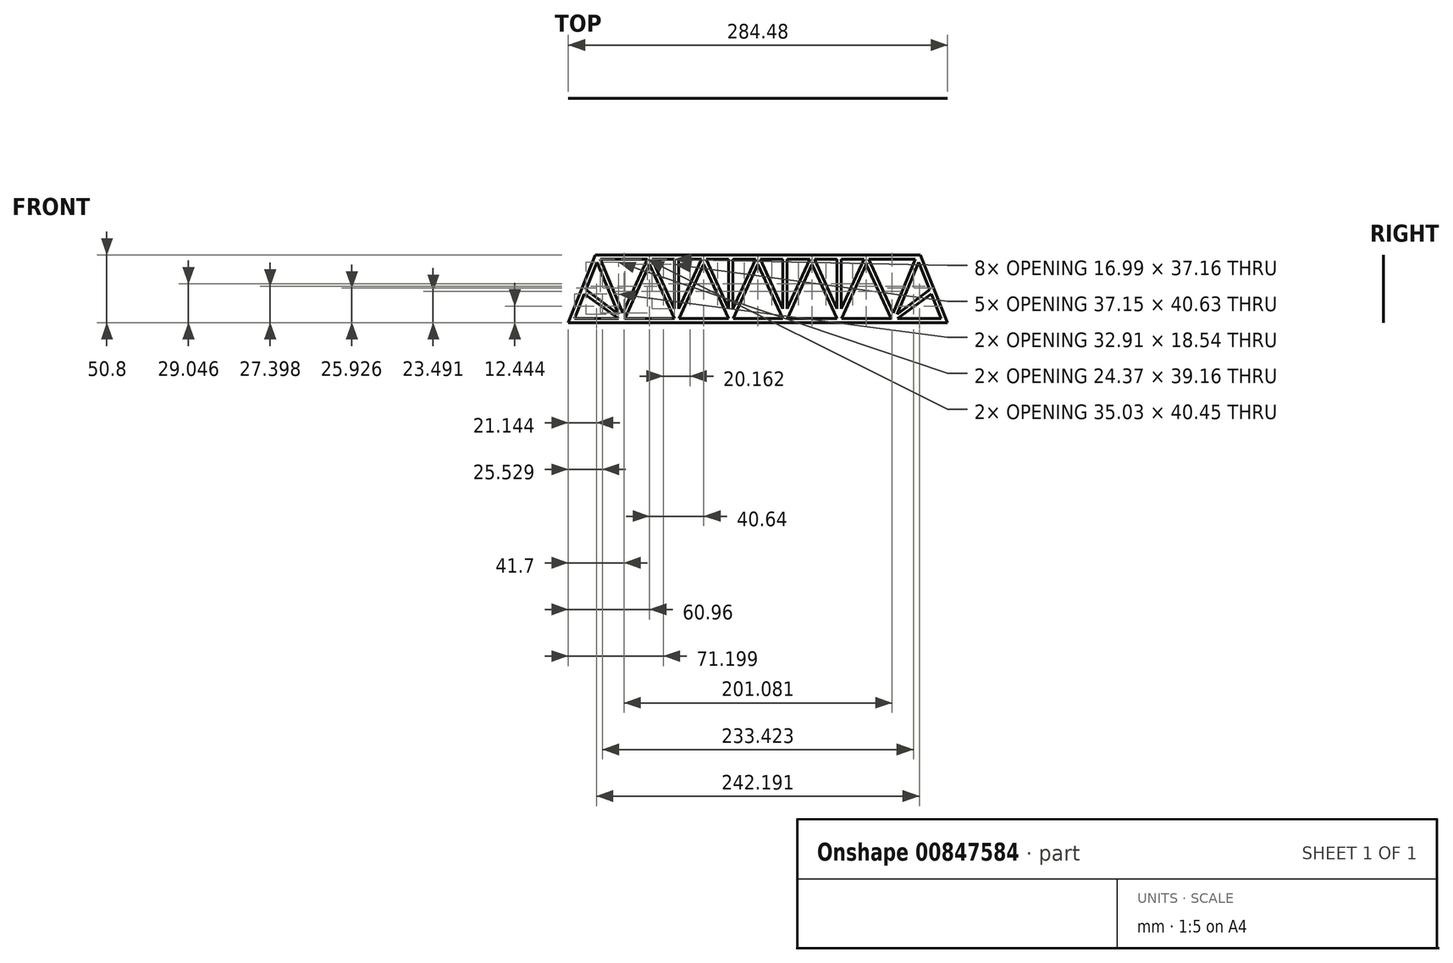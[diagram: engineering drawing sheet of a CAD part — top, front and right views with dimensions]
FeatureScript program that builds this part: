
annotation { "Feature Type Name" : "Feature", "Feature Type Description" : "" }
export const myFeature = defineFeature(function(context is Context, id is Id, definition is map)
    precondition{}
    {
        {
            var Q0;
            Q0=qCreatedBy(makeId("Front.planeOp"),FACE);
            var sketch = newSketch(context, id + "F0", { "sketchPlane" : qUnion([Q0])});
            skLineSegment(sketch, "E0.left", {"start": v(0, 0) * mm, "end": v(0, 50.8) * mm, "construction": true});
            skLineSegment(sketch, "E1", {"start": v(0, 0) * mm, "end": v(-142.24, 0) * mm});
            skLineSegment(sketch, "E2", {"start": v(-121.92, 50.8) * mm, "end": v(-142.24, 0) * mm});
            skLineSegment(sketch, "E3", {"start": v(-121.92, 50.8) * mm, "end": v(0, 50.8) * mm});
            skLineSegment(sketch, "E4.0", {"start": v(-120.62, 45.5) * mm, "end": v(-128.9, 24.81) * mm});
            skLineSegment(sketch, "E5.0", {"start": v(0, 3.18) * mm, "end": v(-18.57, 3.18) * mm});
            skLineSegment(sketch, "E6.0", {"start": v(-118.06, 47.62) * mm, "end": v(-83.03, 47.62) * mm});
            skPoint(sketch, "E7.orphan", {"position": v(1.84, 0) * mm});
            skLineSegment(sketch, "E8", {"start": v(0, 50.8) * mm, "end": v(0, 47.63) * mm});
            skLineSegment(sketch, "E9", {"start": v(0, 3.18) * mm, "end": v(0, 0) * mm});
            skLineSegment(sketch, "E10", {"start": v(-22.07, 3.18) * mm, "end": v(-59.21, 3.18) * mm});
            skLineSegment(sketch, "E11", {"start": v(-62.7, 3.18) * mm, "end": v(-99.85, 3.18) * mm});
            skPoint(sketch, "E12.start.orphan", {"position": v(-40.64, 3.18) * mm});
            skPoint(sketch, "E13.start.orphan", {"position": v(-81.28, 3.18) * mm});
            skLineSegment(sketch, "E14.0", {"start": v(-120.62, 45.5) * mm, "end": v(-104.53, 6.35) * mm});
            skLineSegment(sketch, "E15.0", {"start": v(-118.06, 47.63) * mm, "end": v(-101.52, 7.17) * mm});
            skLineSegment(sketch, "E16.0", {"start": v(-83.03, 47.63) * mm, "end": v(-101.52, 7.17) * mm});
            skLineSegment(sketch, "E17.0", {"start": v(-81.28, 43.8) * mm, "end": v(-99.85, 3.17) * mm});
            skLineSegment(sketch, "E18.0", {"start": v(-81.28, 43.8) * mm, "end": v(-62.7, 3.18) * mm});
            skLineSegment(sketch, "E19.0", {"start": v(-79.53, 47.63) * mm, "end": v(-60.96, 7) * mm});
            skLineSegment(sketch, "E20.0", {"start": v(-59.21, 3.17) * mm, "end": v(-40.64, 43.8) * mm});
            skLineSegment(sketch, "E21.0", {"start": v(-60.96, 7) * mm, "end": v(-42.39, 47.62) * mm});
            skLineSegment(sketch, "E22.0", {"start": v(-22.07, 3.17) * mm, "end": v(-40.64, 43.8) * mm});
            skLineSegment(sketch, "E23.0", {"start": v(-1.75, 47.63) * mm, "end": v(-20.32, 7) * mm});
            skLineSegment(sketch, "E24.0", {"start": v(0, 43.8) * mm, "end": v(-18.57, 3.18) * mm});
            skPoint(sketch, "E25.orphan", {"position": v(-101.6, 3.17) * mm});
            skPoint(sketch, "E26.orphan", {"position": v(-60.96, 3.17) * mm});
            skPoint(sketch, "E27.start.orphan", {"position": v(-81.28, 47.62) * mm});
            skLineSegment(sketch, "E28.trimOffspring", {"start": v(-79.53, 47.62) * mm, "end": v(-42.39, 47.62) * mm});
            skLineSegment(sketch, "E29.trimOffspring", {"start": v(-38.9, 47.62) * mm, "end": v(-1.75, 47.63) * mm});
            skPoint(sketch, "E30.orphan", {"position": v(-40.64, 47.62) * mm});
            skLineSegment(sketch, "E31.trimOffspring", {"start": v(-20.32, 7) * mm, "end": v(-38.9, 47.62) * mm});
            skPoint(sketch, "E32.orphan", {"position": v(-20.32, 3.18) * mm});
            skLineSegment(sketch, "E33", {"start": v(0, 43.8) * mm, "end": v(0, 47.63) * mm});
            skLineSegment(sketch, "E34", {"start": v(-121.92, 50.8) * mm, "end": v(-132.08, 25.4) * mm});
            skLineSegment(sketch, "E35.0", {"start": v(-128.9, 24.81) * mm, "end": v(-104.53, 6.35) * mm});
            skLineSegment(sketch, "E36.trimOffspring", {"start": v(-130.13, 21.71) * mm, "end": v(-137.55, 3.17) * mm});
            skLineSegment(sketch, "E37.trimOffspring", {"start": v(-130.13, 21.71) * mm, "end": v(-104.64, 3.17) * mm});
            skLineSegment(sketch, "E38.trimOffspring", {"start": v(-104.64, 3.18) * mm, "end": v(-137.55, 3.18) * mm});
            skLineSegment(sketch, "E39.trimOffspring", {"start": v(-101.21, 0.68) * mm, "end": v(-100.27, 0) * mm});
            skLineSegment(sketch, "E40", {"start": v(-99.85, 3.18) * mm, "end": v(-147.84, 3.18) * mm});
            skSolve(sketch);
        }
        {
            var Q0;
            Q0 = qSketchRegion(id + "F0", true);
            extrude(context, id + "F1", {"entities" : qUnion([Q0]), "depth" : 1 / 203.2 * mm, "offsetDistance" : 25.4 * mm});
        }
        {
            var Q0;
            Q0=makeQuery(id+"F1.opExtrude","SWEPT_BODY",BODY,{"disambiguationData":[OSD([sQuery(id+"F0.wireOp",EDGE,"E1"),sQuery(id+"F0.wireOp",EDGE,"E2"),sQuery(id+"F0.wireOp",EDGE,"E3"),sQuery(id+"F0.wireOp",EDGE,"E4.0"),sQuery(id+"F0.wireOp",EDGE,"E6.0"),sQuery(id+"F0.wireOp",EDGE,"E8"),sQuery(id+"F0.wireOp",EDGE,"E9"),sQuery(id+"F0.wireOp",EDGE,"E5.0"),sQuery(id+"F0.wireOp",EDGE,"E14.0"),sQuery(id+"F0.wireOp",EDGE,"E15.0"),sQuery(id+"F0.wireOp",EDGE,"E16.0"),sQuery(id+"F0.wireOp",EDGE,"E17.0"),sQuery(id+"F0.wireOp",EDGE,"E18.0"),sQuery(id+"F0.wireOp",EDGE,"E19.0"),sQuery(id+"F0.wireOp",EDGE,"E20.0"),sQuery(id+"F0.wireOp",EDGE,"E21.0"),sQuery(id+"F0.wireOp",EDGE,"E22.0"),sQuery(id+"F0.wireOp",EDGE,"E23.0"),sQuery(id+"F0.wireOp",EDGE,"E24.0"),sQuery(id+"F0.wireOp",EDGE,"9d2a0266-28ce-4e2b-ab8a-bda497a0a275.trimOffspring"),sQuery(id+"F0.wireOp",EDGE,"E11"),sQuery(id+"F0.wireOp",EDGE,"E28.trimOffspring"),sQuery(id+"F0.wireOp",EDGE,"E29.trimOffspring"),sQuery(id+"F0.wireOp",EDGE,"E31.trimOffspring"),sQuery(id+"F0.wireOp",EDGE,"E10"),sQuery(id+"F0.wireOp",EDGE,"E33")])]});
            var Q1;
            Q1=makeQuery(id+"F1.opExtrude","SWEPT_FACE",FACE,{"disambiguationData":[OSD([sQuery(id+"F0.wireOp",EDGE,"E8"),sQuery(id+"F0.wireOp",EDGE,"E33")])]});
            mirror(context, id + "F2", {"operationType" : NewBodyOperationType.ADD, "entities" : qUnion([Q0]), "mirrorPlane" : qUnion([Q1])});
        }
        {
            var Q0;
            Q0=qCreatedBy(makeId("Front.planeOp"),FACE);
            var sketch = newSketch(context, id + "F3", { "sketchPlane" : qUnion([Q0])});
            skLineSegment(sketch, "E41.0", {"start": v(-59.37, 50.8) * mm, "end": v(-59.37, 0) * mm});
            skLineSegment(sketch, "E42.0", {"start": v(-62.55, 50.8) * mm, "end": v(-62.55, 0) * mm});
            skLineSegment(sketch, "E43.0", {"start": v(-21.9, 50.8) * mm, "end": v(-21.9, 0) * mm});
            skLineSegment(sketch, "E44.0", {"start": v(-18.73, 50.8) * mm, "end": v(-18.73, 0) * mm});
            skLineSegment(sketch, "E45.0", {"start": v(59.37, 50.8) * mm, "end": v(59.37, 0) * mm});
            skLineSegment(sketch, "E46.0", {"start": v(62.55, 50.8) * mm, "end": v(62.55, 0) * mm});
            skLineSegment(sketch, "E47", {"start": v(-62.55, 50.8) * mm, "end": v(-59.37, 50.8) * mm});
            skLineSegment(sketch, "E48", {"start": v(-21.9, 50.8) * mm, "end": v(-18.73, 50.8) * mm});
            skLineSegment(sketch, "E49", {"start": v(-62.55, 0) * mm, "end": v(-59.37, 0) * mm});
            skLineSegment(sketch, "E50", {"start": v(-21.9, 0) * mm, "end": v(-18.73, 0) * mm});
            skLineSegment(sketch, "E51", {"start": v(59.37, 0) * mm, "end": v(62.55, 0) * mm});
            skLineSegment(sketch, "E52", {"start": v(59.37, 50.8) * mm, "end": v(62.55, 50.8) * mm});
            skLineSegment(sketch, "E53.0", {"start": v(21.9, 7) * mm, "end": v(21.9, 50.8) * mm});
            skLineSegment(sketch, "E54", {"start": v(21.9, 7) * mm, "end": v(22.07, 0) * mm});
            skLineSegment(sketch, "E55", {"start": v(21.9, 50.8) * mm, "end": v(18.73, 50.8) * mm});
            skLineSegment(sketch, "E56", {"start": v(18.73, 50.8) * mm, "end": v(18.73, 0) * mm});
            skLineSegment(sketch, "E57", {"start": v(18.73, 0) * mm, "end": v(22.07, 0) * mm});
            skPoint(sketch, "E58.end.orphan", {"position": v(20.32, 0) * mm});
            skSolve(sketch);
        }
        {
            var Q0;
            Q0 = qSketchRegion(id + "F3", true);
            extrude(context, id + "F4", {"entities" : qUnion([Q0]), "operationType" : NewBodyOperationType.ADD, "depth" : 1 / 203.2 * mm, "offsetDistance" : 25.4 * mm});
        }
        {
            var Q0;
            Q0=qCreatedBy(makeId("Front.planeOp"),FACE);
            var sketch = newSketch(context, id + "F5", { "sketchPlane" : qUnion([Q0])});
            skLineSegment(sketch, "E59", {"start": v(-43.07, -20.8) * mm, "end": v(14.08, -20.8) * mm});
            skLineSegment(sketch, "E60", {"start": v(14.08, -20.8) * mm, "end": v(14.08, -23.97) * mm});
            skLineSegment(sketch, "E61", {"start": v(14.08, -23.97) * mm, "end": v(10.9, -23.97) * mm});
            skLineSegment(sketch, "E62", {"start": v(10.9, -23.97) * mm, "end": v(10.9, -27.15) * mm});
            skLineSegment(sketch, "E63", {"start": v(10.9, -27.15) * mm, "end": v(-39.9, -27.15) * mm});
            skLineSegment(sketch, "E64", {"start": v(-39.9, -27.15) * mm, "end": v(-39.9, -23.97) * mm});
            skLineSegment(sketch, "E65", {"start": v(-39.9, -23.97) * mm, "end": v(-43.07, -23.97) * mm});
            skLineSegment(sketch, "E66", {"start": v(-43.07, -23.97) * mm, "end": v(-43.07, -20.8) * mm});
            skSolve(sketch);
        }
        {
            var Q0;
            Q0 = qSketchRegion(id + "F5", true);
            extrude(context, id + "F6", {"entities" : qUnion([Q0]), "depth" : 1 / 203.2 * mm, "offsetDistance" : 25.4 * mm});
        }
        {
            var Q0;
            Q0=makeQuery(id+"F6.opExtrude","SWEPT_BODY",BODY,{"disambiguationData":[OSD([sQuery(id+"F5.wireOp",EDGE,"E59"),sQuery(id+"F5.wireOp",EDGE,"E60"),sQuery(id+"F5.wireOp",EDGE,"E61"),sQuery(id+"F5.wireOp",EDGE,"E62"),sQuery(id+"F5.wireOp",EDGE,"E63"),sQuery(id+"F5.wireOp",EDGE,"E64"),sQuery(id+"F5.wireOp",EDGE,"E65"),sQuery(id+"F5.wireOp",EDGE,"E66")])]});
            deleteBodies(context, id + "F7", {"entities" : qUnion([Q0])});
        }
    });
